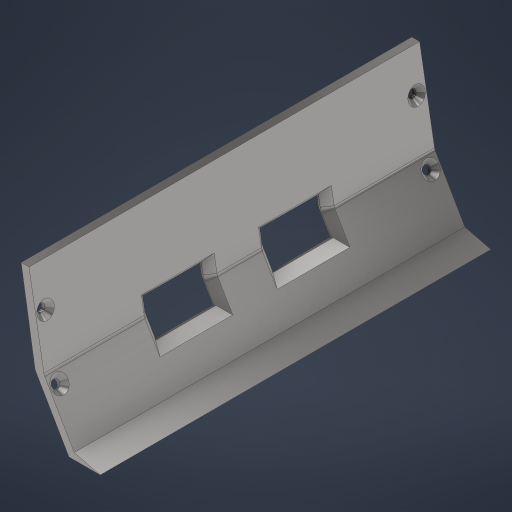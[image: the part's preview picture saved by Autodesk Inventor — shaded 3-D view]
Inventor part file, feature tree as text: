
AUTODESK INVENTOR PART (.ipt)
format: ipt  version: 2024 (Build 280153000, 153)  size: 316,416 bytes
history: native  units: in
note: dims shown in document units (in); Inventor stores cm internally (conversion verified against a paired STEP export)
features: sketch x4, extrude x2, chamfer x2, hole x2
ambient origin geometry x8: Origin, YZ Plane, XZ Plane, XY Plane, X Axis, Y Axis, Z Axis, Center Point
bodies: Solid1 (feature_tree)
feature tree (10):
  extrude  "Extrusion1"  Depth=0.0787in
  extrude  "Extrusion2"  Depth=0.315in
  chamfer  "Chamfer3"  Distance=0.5906in
  sketch  "Sketch7"  dims[d23=0.5906in]
  sketch  "Sketch8"  dims[d24=0.315in d25=0.5906in d26=0.0in d27=0.0in d37=0.6871in d38=0.0787in d39=0.0787in d40=1.378in d41=1.378in d42=0.0709in d43=0.0787in d44=45.0deg d45=0.0787in d46=0.2362in d47=0.1575in d48=0.0787in d49=90.0deg d50=0.315in d51=0.8108in d52=0.0787in d53=0.2362in d54=0.1575in d55=0.0787in d56=90.0deg d57=0.315in d58=0.8108in d59=0.0472in d60=0.0787in d61=45.0deg d62=0.0984in d63=0.0984in]
  hole  "Hole2"  [1 undecoded]
  hole  "Hole3"  [1 undecoded]
  chamfer  "Chamfer4"  Distance=0.0787in
  sketch  "Sketch1"  dims[d0=0.315in d1=120.0deg d3=0.0787in]
  sketch  "Sketch6"  dims[d4=3.937in d5=0.0in d22=0.315in]
note: 2 required parameter values undecoded (feature->parameter linkage not recoverable at this tier; creation-order binding heuristic only, values carry confidence <= 0.55)
